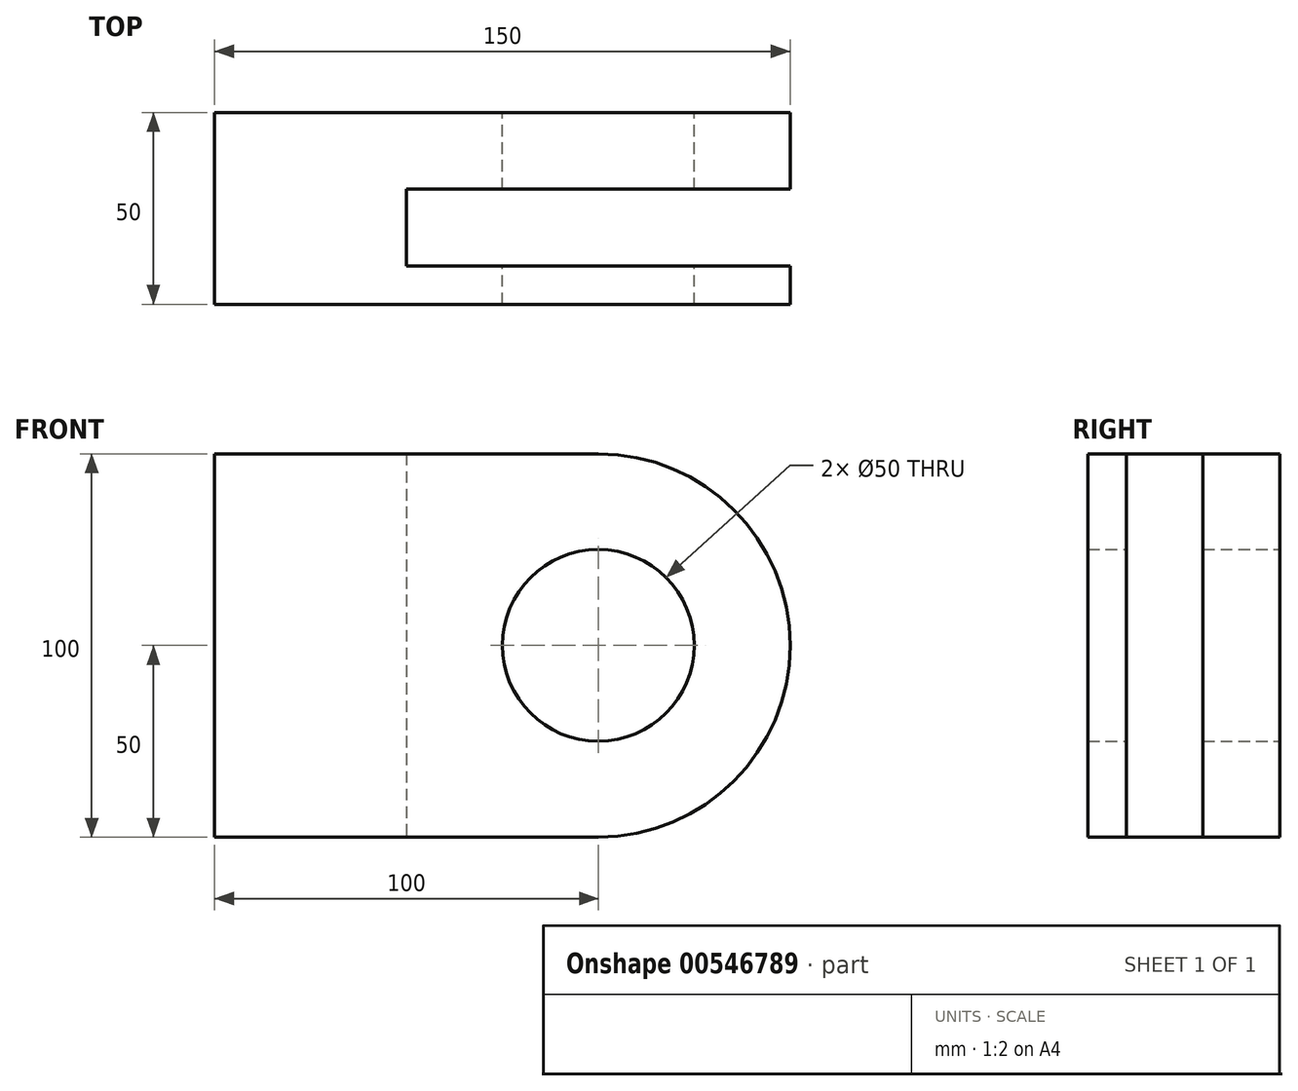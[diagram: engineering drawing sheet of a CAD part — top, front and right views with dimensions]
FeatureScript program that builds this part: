
annotation { "Feature Type Name" : "Feature", "Feature Type Description" : "" }
export const myFeature = defineFeature(function(context is Context, id is Id, definition is map)
    precondition{}
    {
        {
            var Q0;
            Q0=qCreatedBy(makeId("Front.planeOp"),FACE);
            var sketch = newSketch(context, id + "F0", { "sketchPlane" : qUnion([Q0])});
            skCircle(sketch, "E0", {"center": v(0, 0) * mm, "radius": 25 * mm});
            skArc(sketch, "E1", {"start": v(0, -50) * mm, "mid": v(50, 0) * mm, "end": v(0, 50) * mm});
            skLineSegment(sketch, "E2", {"start": v(0, 50) * mm, "end": v(-100, 50) * mm});
            skLineSegment(sketch, "E3", {"start": v(-100, 50) * mm, "end": v(-100, -50) * mm});
            skLineSegment(sketch, "E4", {"start": v(-100, -50) * mm, "end": v(0, -50) * mm});
            skSolve(sketch);
        }
        {
            var Q0;
            Q0=makeQuery(id+"F0.imprint","IMPRINT",FACE,{"disambiguationData":[TD([[makeQuery(id+"F0.imprint","IMPRINT",EDGE,{"derivedFrom":sQuery(id+"F0.wireOp",EDGE,"E0")}),-1.0]])]});
            extrude(context, id + "F1", {"entities" : qUnion([Q0]), "depth" : 20 * mm, "offsetDistance" : 25 * mm});
        }
        {
            var Q0;
            Q0=makeQuery(id+"F1.opExtrude","CAP_FACE",FACE,{"disambiguationData":[OSD([sQuery(id+"F0.wireOp",EDGE,"E0"),sQuery(id+"F0.wireOp",EDGE,"E1"),sQuery(id+"F0.wireOp",EDGE,"E2"),sQuery(id+"F0.wireOp",EDGE,"E3"),sQuery(id+"F0.wireOp",EDGE,"E4")])],"isStart":false});
            cPlane(context, id + "F2", {"entities" : qUnion([Q0]), "cplaneType" : CPlaneType.OFFSET, "offset" : 20 * mm, "width" : 150 * mm, "height" : 150 * mm});
        }
        {
            var Q0;
            Q0=qCreatedBy(id+"F2.planeOp",FACE);
            var sketch = newSketch(context, id + "F3", { "sketchPlane" : qUnion([Q0])});
            skLineSegment(sketch, "E5.0.0", {"start": v(-100, -50) * mm, "end": v(-100, 50) * mm});
            skLineSegment(sketch, "E5.0.1", {"start": v(-100, 50) * mm, "end": v(0, 50) * mm});
            skArc(sketch, "E5.0.2", {"start": v(0, 50) * mm, "mid": v(50, 0) * mm, "end": v(0, -50) * mm});
            skLineSegment(sketch, "E5.0.3", {"start": v(0, -50) * mm, "end": v(-100, -50) * mm});
            skCircle(sketch, "E6.0", {"center": v(0, 0) * mm, "radius": 25 * mm});
            skSolve(sketch);
        }
        {
            var Q0;
            Q0=makeQuery(id+"F3.imprint","IMPRINT",FACE,{"disambiguationData":[TD([[makeQuery(id+"F3.imprint","IMPRINT",EDGE,{"derivedFrom":sQuery(id+"F3.wireOp",EDGE,"E5.0.0")}),-1.0]])]});
            extrude(context, id + "F4", {"entities" : qUnion([Q0]), "depth" : 10 * mm, "offsetDistance" : 25 * mm});
        }
        {
            var Q0;
            Q0=makeQuery(id+"F1.opExtrude","CAP_FACE",FACE,{"disambiguationData":[OSD([sQuery(id+"F0.wireOp",EDGE,"E0"),sQuery(id+"F0.wireOp",EDGE,"E1"),sQuery(id+"F0.wireOp",EDGE,"E2"),sQuery(id+"F0.wireOp",EDGE,"E3"),sQuery(id+"F0.wireOp",EDGE,"E4")])],"isStart":false});
            var sketch = newSketch(context, id + "F5", { "sketchPlane" : qUnion([Q0])});
            skLineSegment(sketch, "E7.bottom", {"start": v(-100, 50) * mm, "end": v(-50, 50) * mm});
            skLineSegment(sketch, "E7.top", {"start": v(-100, -50) * mm, "end": v(-50, -50) * mm});
            skLineSegment(sketch, "E7.left", {"start": v(-100, 50) * mm, "end": v(-100, -50) * mm});
            skLineSegment(sketch, "E7.right", {"start": v(-50, 50) * mm, "end": v(-50, -50) * mm});
            skSolve(sketch);
        }
        {
            var Q0;
            Q0=makeQuery(id+"F5.imprint","IMPRINT",FACE,{"disambiguationData":[TD([[makeQuery(id+"F5.imprint","IMPRINT",EDGE,{"derivedFrom":sQuery(id+"F5.wireOp",EDGE,"E7.bottom")}),1.0]])]});
            extrude(context, id + "F6", {"entities" : qUnion([Q0]), "operationType" : NewBodyOperationType.ADD, "endBound" : BoundingType.UP_TO_NEXT, "depth" : 25 * mm, "offsetDistance" : 25 * mm});
        }
    });
